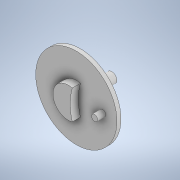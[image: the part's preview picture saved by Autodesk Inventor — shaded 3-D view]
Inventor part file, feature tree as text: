
AUTODESK INVENTOR PART (.ipt)
format: ipt  version: 2022 (Build 260153000, 153)  size: 141,824 bytes
history: native  units: in
note: dims shown in document units (in); Inventor stores cm internally (conversion verified against a paired STEP export)
features: extrude x6, sketch x6
ambient origin geometry x8: Origin, YZ Plane, XZ Plane, XY Plane, X Axis, Y Axis, Z Axis, Center Point
bodies: Solid1 (feature_tree)
feature tree (12):
  extrude  "Extrusion1"  Depth=0.1575in TaperAngle=0.0deg
  extrude  "Extrusion2"  Depth=0.315in TaperAngle=0.0deg
  sketch  "Sketch3"  dims[d6=0.1181in d9=0.3937in]
  extrude  "Extrusion4"  Depth=0.3937in
  extrude  "Extrusion5"  Depth=0.1969in
  extrude  "Extrusion6"  Depth=0.1181in TaperAngle=0.0deg
  extrude  "Extrusion7"  Depth=0.0787in TaperAngle=0.0deg
  sketch  "Sketch1"  dims[d0=1.5748in d1=0.1575in d2=0.0in]
  sketch  "Sketch2"  dims[d3=0.5906in d4=0.315in d5=0.0in]
  sketch  "Sketch4"  dims[d10=0.2362in d11=0.0in d12=0.1969in]
  sketch  "Sketch5"  dims[d13=0.1181in d14=0.9843in d15=0.0in]
  sketch  "Sketch6"  dims[d16=0.0787in d17=0.9843in d18=0.0in d19=0.315in d20=0.0in]
